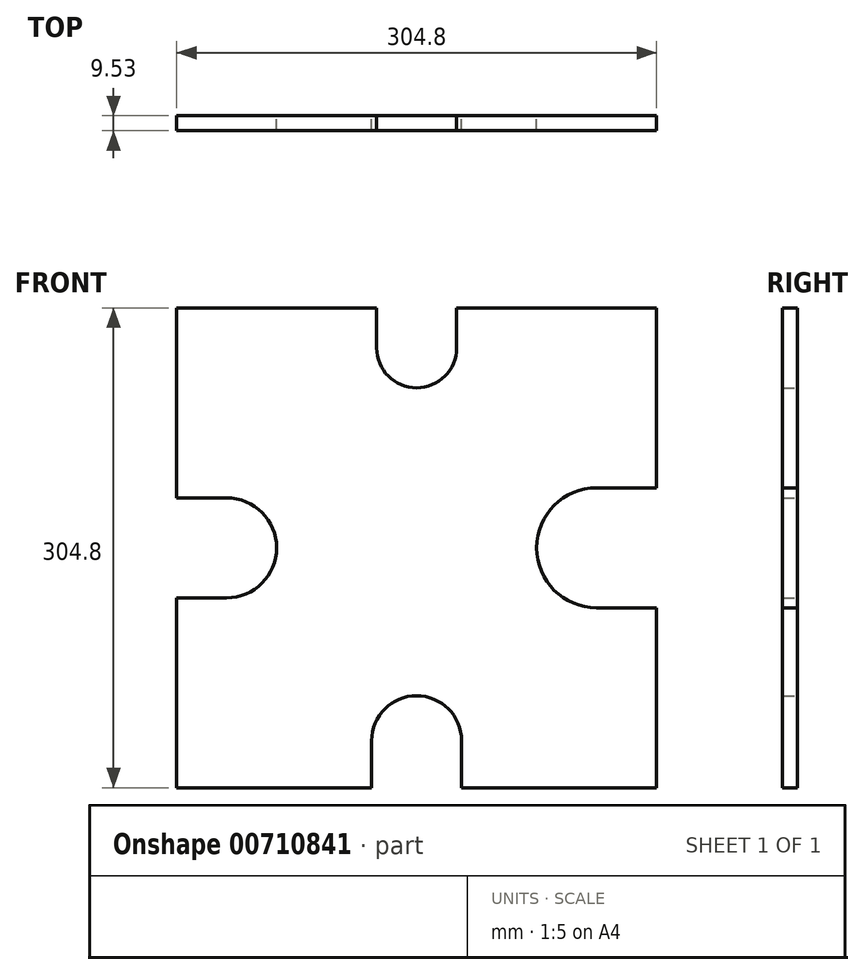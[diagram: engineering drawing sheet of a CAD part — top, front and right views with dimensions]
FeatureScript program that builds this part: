
annotation { "Feature Type Name" : "Feature", "Feature Type Description" : "" }
export const myFeature = defineFeature(function(context is Context, id is Id, definition is map)
    precondition{}
    {
        {
            var Q0;
            Q0=qCreatedBy(makeId("Front.planeOp"),FACE);
            var sketch = newSketch(context, id + "F0", { "sketchPlane" : qUnion([Q0])});
            skLineSegment(sketch, "E0.bottom", {"start": v(152.4, 152.4) * mm, "end": v(-152.4, 152.4) * mm});
            skLineSegment(sketch, "E0.top", {"start": v(152.4, -152.4) * mm, "end": v(-152.4, -152.4) * mm});
            skLineSegment(sketch, "E0.left", {"start": v(152.4, 152.4) * mm, "end": v(152.4, -152.4) * mm});
            skLineSegment(sketch, "E0.right", {"start": v(-152.4, 152.4) * mm, "end": v(-152.4, -152.4) * mm});
            skPoint(sketch, "E0.middle", {"position": v(0, 0) * mm});
            skLineSegment(sketch, "E1.bottom", {"start": v(-25.4, 152.4) * mm, "end": v(25.4, 152.4) * mm});
            skLineSegment(sketch, "E1.top", {"start": v(-25.4, 127) * mm, "end": v(25.4, 127) * mm});
            skLineSegment(sketch, "E1.left", {"start": v(-25.4, 152.4) * mm, "end": v(-25.4, 127) * mm});
            skLineSegment(sketch, "E1.right", {"start": v(25.4, 152.4) * mm, "end": v(25.4, 127) * mm});
            skArc(sketch, "E2", {"start": v(25.4, 127) * mm, "mid": v(0, 101.6) * mm, "end": v(-25.4, 127) * mm});
            skLineSegment(sketch, "E3.bottom", {"start": v(-152.4, 31.75) * mm, "end": v(-120.65, 31.75) * mm});
            skLineSegment(sketch, "E3.top", {"start": v(-152.4, -31.75) * mm, "end": v(-120.65, -31.75) * mm});
            skLineSegment(sketch, "E3.left", {"start": v(-152.4, 31.75) * mm, "end": v(-152.4, -31.75) * mm});
            skLineSegment(sketch, "E3.right", {"start": v(-120.65, 31.75) * mm, "end": v(-120.65, -31.75) * mm});
            skArc(sketch, "E4", {"start": v(-120.65, -31.75) * mm, "mid": v(-88.9, 0) * mm, "end": v(-120.65, 31.75) * mm});
            skLineSegment(sketch, "E5.bottom", {"start": v(-28.57, -152.4) * mm, "end": v(28.57, -152.4) * mm});
            skLineSegment(sketch, "E5.top", {"start": v(-28.57, -122.55) * mm, "end": v(28.57, -122.55) * mm});
            skLineSegment(sketch, "E5.left", {"start": v(-28.57, -152.4) * mm, "end": v(-28.57, -122.55) * mm});
            skLineSegment(sketch, "E5.right", {"start": v(28.58, -152.4) * mm, "end": v(28.58, -122.55) * mm});
            skLineSegment(sketch, "E6.bottom", {"start": v(152.4, 38.1) * mm, "end": v(114.3, 38.1) * mm});
            skLineSegment(sketch, "E6.top", {"start": v(152.4, -38.1) * mm, "end": v(114.3, -38.1) * mm});
            skLineSegment(sketch, "E6.left", {"start": v(152.4, 38.1) * mm, "end": v(152.4, -38.1) * mm});
            skLineSegment(sketch, "E6.right", {"start": v(114.3, 38.1) * mm, "end": v(114.3, -38.1) * mm});
            skArc(sketch, "E7", {"start": v(28.58, -122.55) * mm, "mid": v(0, -93.98) * mm, "end": v(-28.58, -122.55) * mm});
            skArc(sketch, "E8", {"start": v(114.3, 38.1) * mm, "mid": v(76.2, 0) * mm, "end": v(114.3, -38.1) * mm});
            skSolve(sketch);
        }
        {
            var Q0;
            {var subQ0=sQuery(id+"F0.wireOp",EDGE,"E1.left");Q0=makeQuery(id+"F0.imprint","IMPRINT",FACE,{"disambiguationData":[TD([[makeQuery(id+"F0.imprint","IMPRINT",EDGE,{"derivedFrom":subQ0}),-1.0]])]});}
            extrude(context, id + "F1", {"entities" : qUnion([Q0]), "depth" : 9.52 * mm, "offsetDistance" : 25.4 * mm});
        }
    });
